# Revit family: Holyoake_-_SFRA_Swirl_Fixed_Round_Aluminium
name_source: partatom
category: Air Terminals
revit_build: Autodesk Revit 2014 (Build: 20130308_1515(x64)
units: mm (PartAtom-declared; Revit-internal decimal feet)

## types (5) — shared parameters
Blade Offset = 64 mm  [stored 0.209974 ft]
Default Elevation = 1219 mm
Manufacturer = Holyoake
Model = SFRA
Type Comments = Swirl Fixed Round Aluminium
URL = http://www.productspec.net

## per-type parameters (varying)
| type | A | B | C | D | Radius |
| 200mm | 195 mm  [stored 0.639764 ft] | 299 mm  [stored 0.980971 ft] | 65 mm  [stored 0.213255 ft] | 33 mm  [stored 0.108268 ft] | 117 mm |
| 250mm | 245 mm | 362 mm | 70 mm | 35 mm | 146 mm  [stored 0.479003 ft] |
| 300mm | 295 mm | 425 mm | 90 mm | 37 mm | 176 mm |
| 350mm | 345 mm | 488 mm | 110 mm | 38 mm | 206 mm  [stored 0.675853 ft] |
| 400mm | 395 mm  [stored 1.29593 ft] | 550 mm | 130 mm  [stored 0.426509 ft] | 40 mm  [stored 0.131234 ft] | 235 mm  [stored 0.770997 ft] |

note: [stored X ft] marks values corroborated as IEEE doubles in the binary element streams (Revit-internal decimal feet)

## geometry (parser evidence)
native form markers: Revolve x4, Sweep x6
no freeform markers — native parametric forms only
